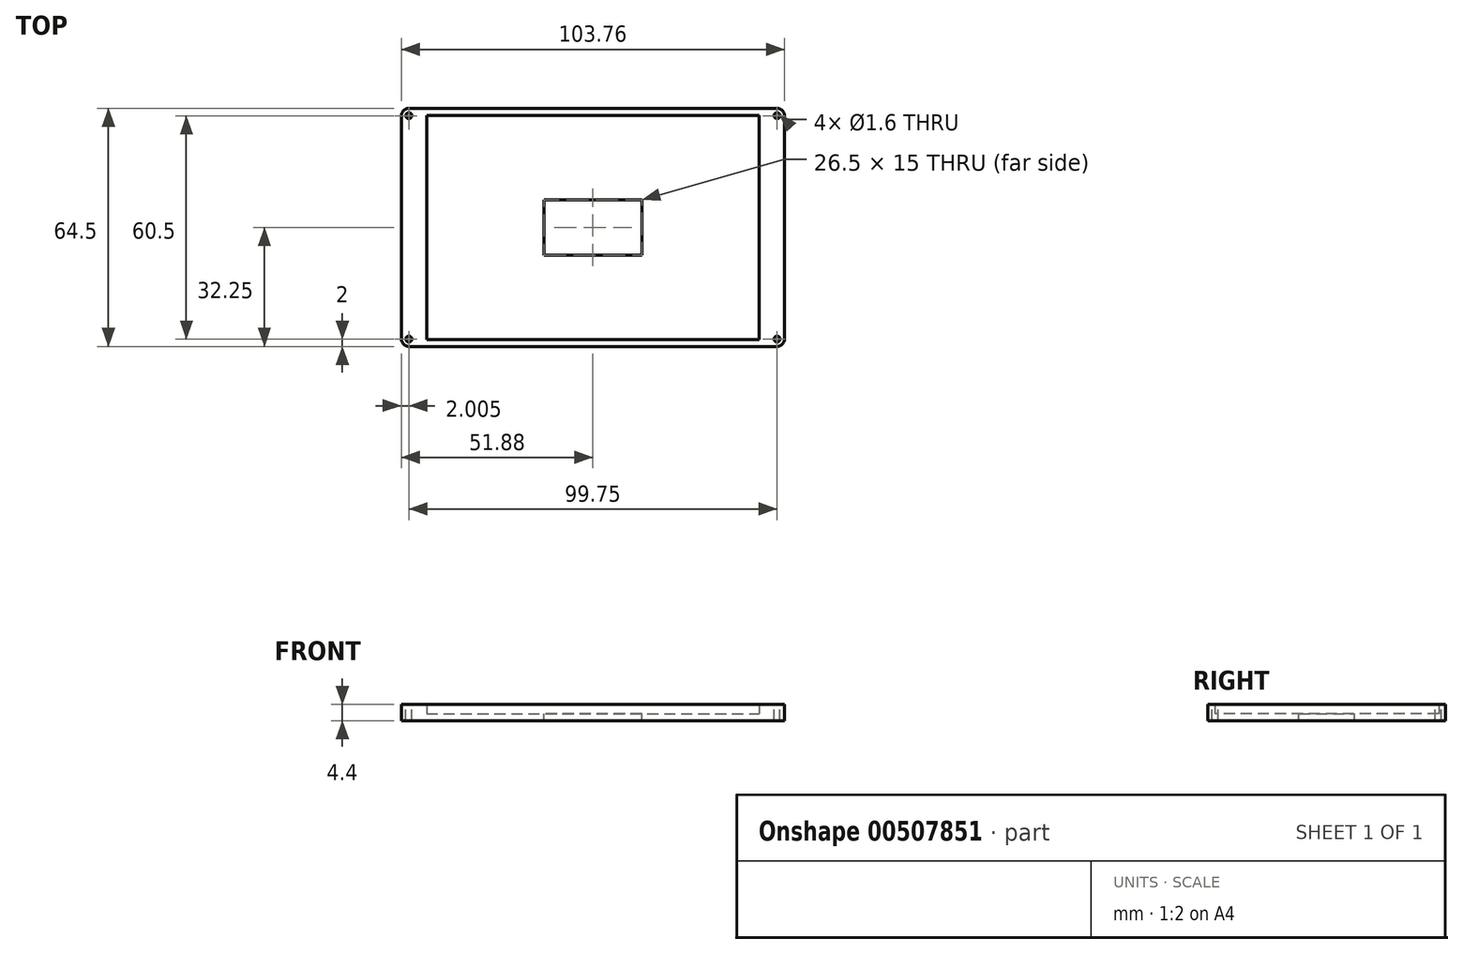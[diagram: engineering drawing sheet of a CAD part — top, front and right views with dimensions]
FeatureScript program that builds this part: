
annotation { "Feature Type Name" : "Feature", "Feature Type Description" : "" }
export const myFeature = defineFeature(function(context is Context, id is Id, definition is map)
    precondition{}
    {
        {
            var Q0;
            Q0=qCreatedBy(makeId("Top.planeOp"),FACE);
            var sketch = newSketch(context, id + "F0", { "sketchPlane" : qUnion([Q0])});
            skLineSegment(sketch, "E0.bottom", {"start": v(-51.88, 32.25) * mm, "end": v(51.88, 32.25) * mm});
            skLineSegment(sketch, "E0.top", {"start": v(-51.88, -32.25) * mm, "end": v(51.88, -32.25) * mm});
            skLineSegment(sketch, "E0.left", {"start": v(-51.88, 32.25) * mm, "end": v(-51.88, -32.25) * mm});
            skLineSegment(sketch, "E0.right", {"start": v(51.88, 32.25) * mm, "end": v(51.88, -32.25) * mm});
            skPoint(sketch, "E0.middle", {"position": v(0, 0) * mm});
            skSolve(sketch);
        }
        {
            var Q0;
            Q0=makeQuery(id+"F0.imprint","IMPRINT",FACE,{"disambiguationData":[TD([[makeQuery(id+"F0.imprint","IMPRINT",EDGE,{"derivedFrom":sQuery(id+"F0.wireOp",EDGE,"E0.bottom")}),-1.0]])]});
            extrude(context, id + "F1", {"entities" : qUnion([Q0]), "endBound" : BoundingType.SYMMETRIC, "depth" : 4.4 * mm});
        }
        {
            var Q0;
            Q0=makeQuery(id+"F1.opExtrude","CAP_FACE",FACE,{"disambiguationData":[OSD([sQuery(id+"F0.wireOp",EDGE,"E0.bottom"),sQuery(id+"F0.wireOp",EDGE,"E0.top"),sQuery(id+"F0.wireOp",EDGE,"E0.left"),sQuery(id+"F0.wireOp",EDGE,"E0.right")])],"isStart":false});
            shell(context, id + "F2", {"entities" : qUnion([Q0]), "thickness" : 1.9 * mm});
        }
        {
            var Q0;
            Q0=qCreatedBy(makeId("Top.planeOp"),FACE);
            var sketch = newSketch(context, id + "F3", { "sketchPlane" : qUnion([Q0])});
            skLineSegment(sketch, "E1.bottom", {"start": v(13.25, -7.5) * mm, "end": v(-13.25, -7.5) * mm});
            skLineSegment(sketch, "E1.top", {"start": v(13.25, 7.5) * mm, "end": v(-13.25, 7.5) * mm});
            skLineSegment(sketch, "E1.left", {"start": v(13.25, -7.5) * mm, "end": v(13.25, 7.5) * mm});
            skLineSegment(sketch, "E1.right", {"start": v(-13.25, -7.5) * mm, "end": v(-13.25, 7.5) * mm});
            skPoint(sketch, "E1.middle", {"position": v(0, 0) * mm});
            skSolve(sketch);
        }
        {
            var Q0;
            Q0=qSketchRegion(id+"F3",true);
            extrude(context, id + "F4", {"entities" : qUnion([Q0]), "operationType" : NewBodyOperationType.REMOVE, "endBound" : BoundingType.SYMMETRIC, "oppositeDirection" : true, "depth" : 25.4 * mm});
        }
        {
            var Q0;
            Q0=makeQuery(id+"F1.opExtrude","SWEPT_EDGE",EDGE,{"disambiguationData":[OSD([sQuery(id+"F0.wireOp",EDGE,"E0.bottom"),sQuery(id+"F0.wireOp",EDGE,"E0.left")])]});
            fillet(context, id + "F5", {"entities" : qUnion([Q0]), "radius" : 2 * mm, "tangentPropagation" : true, "allowEdgeOverflow" : false});
        }
        {
            var Q0;
            Q0=makeQuery(id+"F1.opExtrude","SWEPT_EDGE",EDGE,{"disambiguationData":[OSD([sQuery(id+"F0.wireOp",EDGE,"E0.top"),sQuery(id+"F0.wireOp",EDGE,"E0.left")])]});
            var Q1;
            Q1=makeQuery(id+"F1.opExtrude","SWEPT_EDGE",EDGE,{"disambiguationData":[OSD([sQuery(id+"F0.wireOp",EDGE,"E0.top"),sQuery(id+"F0.wireOp",EDGE,"E0.right")])]});
            var Q2;
            Q2=makeQuery(id+"F1.opExtrude","SWEPT_EDGE",EDGE,{"disambiguationData":[OSD([sQuery(id+"F0.wireOp",EDGE,"E0.bottom"),sQuery(id+"F0.wireOp",EDGE,"E0.right")])]});
            fillet(context, id + "F6", {"entities" : qUnion([Q0, Q1, Q2]), "radius" : 2 * mm, "tangentPropagation" : true, "allowEdgeOverflow" : false});
        }
        {
            var Q0;
            Q0=makeQuery(id+"F2.opShell","OFFSET_FACE",FACE,{"disambiguationData":[OSD([sQuery(id+"F0.wireOp",EDGE,"E0.bottom"),sQuery(id+"F0.wireOp",EDGE,"E0.top"),sQuery(id+"F0.wireOp",EDGE,"E0.left"),sQuery(id+"F0.wireOp",EDGE,"E0.right")])]});
            var sketch = newSketch(context, id + "F7", { "sketchPlane" : qUnion([Q0])});
            skLineSegment(sketch, "E2.bottom", {"start": v(-49.98, -30.35) * mm, "end": v(-45.08, -30.35) * mm});
            skLineSegment(sketch, "E2.top", {"start": v(-49.98, 30.35) * mm, "end": v(-45.08, 30.35) * mm});
            skLineSegment(sketch, "E2.left", {"start": v(-49.98, -30.35) * mm, "end": v(-49.98, 30.35) * mm});
            skLineSegment(sketch, "E2.right", {"start": v(-45.08, -30.35) * mm, "end": v(-45.08, 30.35) * mm});
            skSolve(sketch);
        }
        {
            var Q0;
            Q0 = qSketchRegion(id + "F7", true);
            extrude(context, id + "F8", {"entities" : qUnion([Q0]), "operationType" : NewBodyOperationType.ADD, "depth" : 2.5 * mm});
        }
        {
            var Q0;
            Q0=makeQuery(id+"F2.opShell","OFFSET_FACE",FACE,{"disambiguationData":[OSD([sQuery(id+"F0.wireOp",EDGE,"E0.bottom"),sQuery(id+"F0.wireOp",EDGE,"E0.top"),sQuery(id+"F0.wireOp",EDGE,"E0.left"),sQuery(id+"F0.wireOp",EDGE,"E0.right")])]});
            var sketch = newSketch(context, id + "F9", { "sketchPlane" : qUnion([Q0])});
            skLineSegment(sketch, "E3.bottom", {"start": v(49.98, 30.35) * mm, "end": v(45.08, 30.35) * mm});
            skLineSegment(sketch, "E3.top", {"start": v(49.98, -30.35) * mm, "end": v(45.08, -30.35) * mm});
            skLineSegment(sketch, "E3.left", {"start": v(49.98, 30.35) * mm, "end": v(49.98, -30.35) * mm});
            skLineSegment(sketch, "E3.right", {"start": v(45.08, 30.35) * mm, "end": v(45.08, -30.35) * mm});
            skSolve(sketch);
        }
        {
            var Q0;
            Q0 = qSketchRegion(id + "F9", true);
            extrude(context, id + "F10", {"entities" : qUnion([Q0]), "operationType" : NewBodyOperationType.ADD, "depth" : 2.5 * mm});
        }
        {
            var Q0;
            Q0=makeQuery(id+"F10.boolean.opBoolean","MERGE",FACE,{"derivedFrom":[makeQuery(id+"F8.boolean.opBoolean","MERGE",FACE,{"derivedFrom":[makeQuery(id+"F1.opExtrude","CAP_FACE",FACE,{"disambiguationData":[OSD([sQuery(id+"F0.wireOp",EDGE,"E0.bottom"),sQuery(id+"F0.wireOp",EDGE,"E0.top"),sQuery(id+"F0.wireOp",EDGE,"E0.left"),sQuery(id+"F0.wireOp",EDGE,"E0.right")])],"isStart":false}),makeQuery(id+"F8.opExtrude","CAP_FACE",FACE,{"disambiguationData":[OSD([sQuery(id+"F7.wireOp",EDGE,"E2.bottom"),sQuery(id+"F7.wireOp",EDGE,"E2.top"),sQuery(id+"F7.wireOp",EDGE,"E2.left"),sQuery(id+"F7.wireOp",EDGE,"E2.right")])],"isStart":false})]}),makeQuery(id+"F10.opExtrude","CAP_FACE",FACE,{"disambiguationData":[OSD([sQuery(id+"F9.wireOp",EDGE,"E3.bottom"),sQuery(id+"F9.wireOp",EDGE,"E3.top"),sQuery(id+"F9.wireOp",EDGE,"E3.left"),sQuery(id+"F9.wireOp",EDGE,"E3.right")])],"isStart":false})]});
            var sketch = newSketch(context, id + "F11", { "sketchPlane" : qUnion([Q0])});
            skCircle(sketch, "E4", {"center": v(49.88, -30.25) * mm, "radius": 0.8 * mm});
            skSolve(sketch);
        }
        {
            var Q0;
            Q0 = qSketchRegion(id + "F11", true);
            extrude(context, id + "F12", {"entities" : qUnion([Q0]), "operationType" : NewBodyOperationType.REMOVE, "oppositeDirection" : true, "depth" : 25.4 * mm});
        }
        {
            var Q0;
            Q0=makeQuery(id+"F10.boolean.opBoolean","MERGE",FACE,{"derivedFrom":[makeQuery(id+"F8.boolean.opBoolean","MERGE",FACE,{"derivedFrom":[makeQuery(id+"F1.opExtrude","CAP_FACE",FACE,{"disambiguationData":[OSD([sQuery(id+"F0.wireOp",EDGE,"E0.bottom"),sQuery(id+"F0.wireOp",EDGE,"E0.top"),sQuery(id+"F0.wireOp",EDGE,"E0.left"),sQuery(id+"F0.wireOp",EDGE,"E0.right")])],"isStart":false}),makeQuery(id+"F8.opExtrude","CAP_FACE",FACE,{"disambiguationData":[OSD([sQuery(id+"F7.wireOp",EDGE,"E2.bottom"),sQuery(id+"F7.wireOp",EDGE,"E2.top"),sQuery(id+"F7.wireOp",EDGE,"E2.left"),sQuery(id+"F7.wireOp",EDGE,"E2.right")])],"isStart":false})]}),makeQuery(id+"F10.opExtrude","CAP_FACE",FACE,{"disambiguationData":[OSD([sQuery(id+"F9.wireOp",EDGE,"E3.bottom"),sQuery(id+"F9.wireOp",EDGE,"E3.top"),sQuery(id+"F9.wireOp",EDGE,"E3.left"),sQuery(id+"F9.wireOp",EDGE,"E3.right")])],"isStart":false})]});
            var sketch = newSketch(context, id + "F13", { "sketchPlane" : qUnion([Q0])});
            skCircle(sketch, "E5", {"center": v(49.88, 30.25) * mm, "radius": 0.8 * mm});
            skSolve(sketch);
        }
        {
            var Q0;
            Q0 = qSketchRegion(id + "F13", true);
            extrude(context, id + "F14", {"entities" : qUnion([Q0]), "operationType" : NewBodyOperationType.REMOVE, "oppositeDirection" : true, "depth" : 25.4 * mm});
        }
        {
            var Q0;
            Q0=makeQuery(id+"F10.boolean.opBoolean","MERGE",FACE,{"derivedFrom":[makeQuery(id+"F8.boolean.opBoolean","MERGE",FACE,{"derivedFrom":[makeQuery(id+"F1.opExtrude","CAP_FACE",FACE,{"disambiguationData":[OSD([sQuery(id+"F0.wireOp",EDGE,"E0.bottom"),sQuery(id+"F0.wireOp",EDGE,"E0.top"),sQuery(id+"F0.wireOp",EDGE,"E0.left"),sQuery(id+"F0.wireOp",EDGE,"E0.right")])],"isStart":false}),makeQuery(id+"F8.opExtrude","CAP_FACE",FACE,{"disambiguationData":[OSD([sQuery(id+"F7.wireOp",EDGE,"E2.bottom"),sQuery(id+"F7.wireOp",EDGE,"E2.top"),sQuery(id+"F7.wireOp",EDGE,"E2.left"),sQuery(id+"F7.wireOp",EDGE,"E2.right")])],"isStart":false})]}),makeQuery(id+"F10.opExtrude","CAP_FACE",FACE,{"disambiguationData":[OSD([sQuery(id+"F9.wireOp",EDGE,"E3.bottom"),sQuery(id+"F9.wireOp",EDGE,"E3.top"),sQuery(id+"F9.wireOp",EDGE,"E3.left"),sQuery(id+"F9.wireOp",EDGE,"E3.right")])],"isStart":false})]});
            var sketch = newSketch(context, id + "F15", { "sketchPlane" : qUnion([Q0])});
            skCircle(sketch, "E6", {"center": v(-49.88, -30.25) * mm, "radius": 0.8 * mm});
            skSolve(sketch);
        }
        {
            var Q0;
            Q0 = qSketchRegion(id + "F15", true);
            extrude(context, id + "F16", {"entities" : qUnion([Q0]), "operationType" : NewBodyOperationType.REMOVE, "oppositeDirection" : true, "depth" : 25.4 * mm});
        }
        {
            var Q0;
            Q0=makeQuery(id+"F10.boolean.opBoolean","MERGE",FACE,{"derivedFrom":[makeQuery(id+"F8.boolean.opBoolean","MERGE",FACE,{"derivedFrom":[makeQuery(id+"F1.opExtrude","CAP_FACE",FACE,{"disambiguationData":[OSD([sQuery(id+"F0.wireOp",EDGE,"E0.bottom"),sQuery(id+"F0.wireOp",EDGE,"E0.top"),sQuery(id+"F0.wireOp",EDGE,"E0.left"),sQuery(id+"F0.wireOp",EDGE,"E0.right")])],"isStart":false}),makeQuery(id+"F8.opExtrude","CAP_FACE",FACE,{"disambiguationData":[OSD([sQuery(id+"F7.wireOp",EDGE,"E2.bottom"),sQuery(id+"F7.wireOp",EDGE,"E2.top"),sQuery(id+"F7.wireOp",EDGE,"E2.left"),sQuery(id+"F7.wireOp",EDGE,"E2.right")])],"isStart":false})]}),makeQuery(id+"F10.opExtrude","CAP_FACE",FACE,{"disambiguationData":[OSD([sQuery(id+"F9.wireOp",EDGE,"E3.bottom"),sQuery(id+"F9.wireOp",EDGE,"E3.top"),sQuery(id+"F9.wireOp",EDGE,"E3.left"),sQuery(id+"F9.wireOp",EDGE,"E3.right")])],"isStart":false})]});
            var sketch = newSketch(context, id + "F17", { "sketchPlane" : qUnion([Q0])});
            skCircle(sketch, "E7", {"center": v(-49.87, 30.25) * mm, "radius": 0.8 * mm});
            skSolve(sketch);
        }
        {
            var Q0;
            Q0 = qSketchRegion(id + "F17", true);
            extrude(context, id + "F18", {"entities" : qUnion([Q0]), "operationType" : NewBodyOperationType.REMOVE, "oppositeDirection" : true, "depth" : 25.4 * mm});
        }
    });
